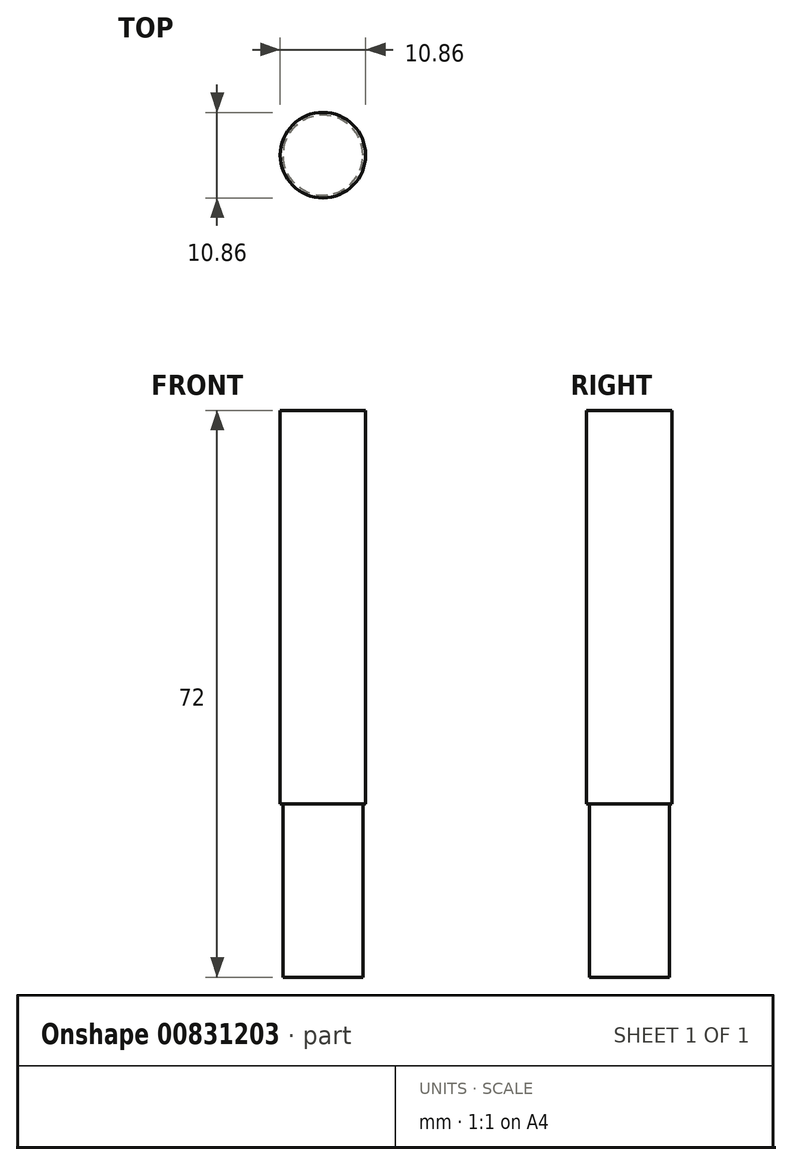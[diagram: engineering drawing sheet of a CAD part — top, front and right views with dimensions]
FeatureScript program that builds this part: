
annotation { "Feature Type Name" : "Feature", "Feature Type Description" : "" }
export const myFeature = defineFeature(function(context is Context, id is Id, definition is map)
    precondition{}
    {
        {
            var Q0;
            Q0=qCreatedBy(makeId("Front.planeOp"),FACE);
            var sketch = newSketch(context, id + "F0", { "sketchPlane" : qUnion([Q0])});
            skLineSegment(sketch, "E0", {"start": v(0, 0) * mm, "end": v(5.42, 0) * mm});
            skLineSegment(sketch, "E1", {"start": v(5.42, 0) * mm, "end": v(5.42, -50) * mm});
            skLineSegment(sketch, "E2", {"start": v(5.42, -50) * mm, "end": v(5.37, -50) * mm});
            skLineSegment(sketch, "E3", {"start": v(5.07, -50.3) * mm, "end": v(5.08, -72) * mm});
            skLineSegment(sketch, "E4", {"start": v(5.08, -72) * mm, "end": v(0, -72) * mm});
            skLineSegment(sketch, "E5", {"start": v(0, -72) * mm, "end": v(0, 0) * mm});
            skPoint(sketch, "E6.visualSharp", {"position": v(5.07, -50) * mm});
            skArc(sketch, "E6.filletArc", {"start": v(5.37, -50) * mm, "mid": v(5.16, -50.09) * mm, "end": v(5.07, -50.3) * mm});
            skSolve(sketch);
        }
        {
            var Q0;
            Q0=makeQuery(id+"F0.imprint","IMPRINT",FACE,{"disambiguationData":[TD([[makeQuery(id+"F0.imprint","IMPRINT",EDGE,{"derivedFrom":sQuery(id+"F0.wireOp",EDGE,"E0")}),-1.0]])]});
            var Q1;
            Q1=sQuery(id+"F0.wireOp",EDGE,"E5");
            revolve(context, id + "F1", {"surfaceOperationType" : NewSurfaceOperationType.NEW, "entities" : qUnion([Q0]), "axis" : qUnion([Q1]), "revolveType" : RevolveType.FULL});
        }
    });
